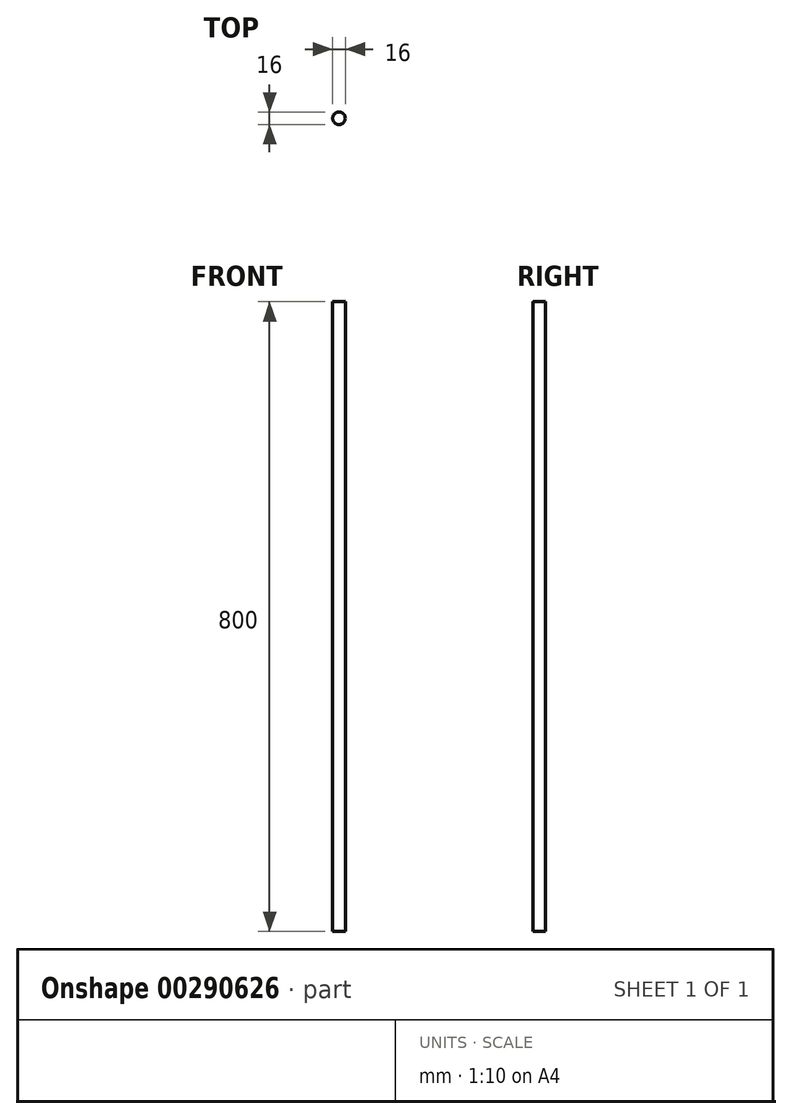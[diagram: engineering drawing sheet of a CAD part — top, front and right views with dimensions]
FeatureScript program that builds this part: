
annotation { "Feature Type Name" : "Feature", "Feature Type Description" : "" }
export const myFeature = defineFeature(function(context is Context, id is Id, definition is map)
    precondition{}
    {
        {
            var Q0;
            Q0=qCreatedBy(makeId("Top.planeOp"),FACE);
            var sketch = newSketch(context, id + "F0", { "sketchPlane" : qUnion([Q0])});
            skCircle(sketch, "E0", {"center": v(0, 0) * mm, "radius": 8 * mm});
            skSolve(sketch);
        }
        {
            var Q0;
            Q0=qSketchRegion(id+"F0",true);
            extrude(context, id + "F1", {"entities" : qUnion([Q0]), "depth" : 800 * mm});
        }
    });
